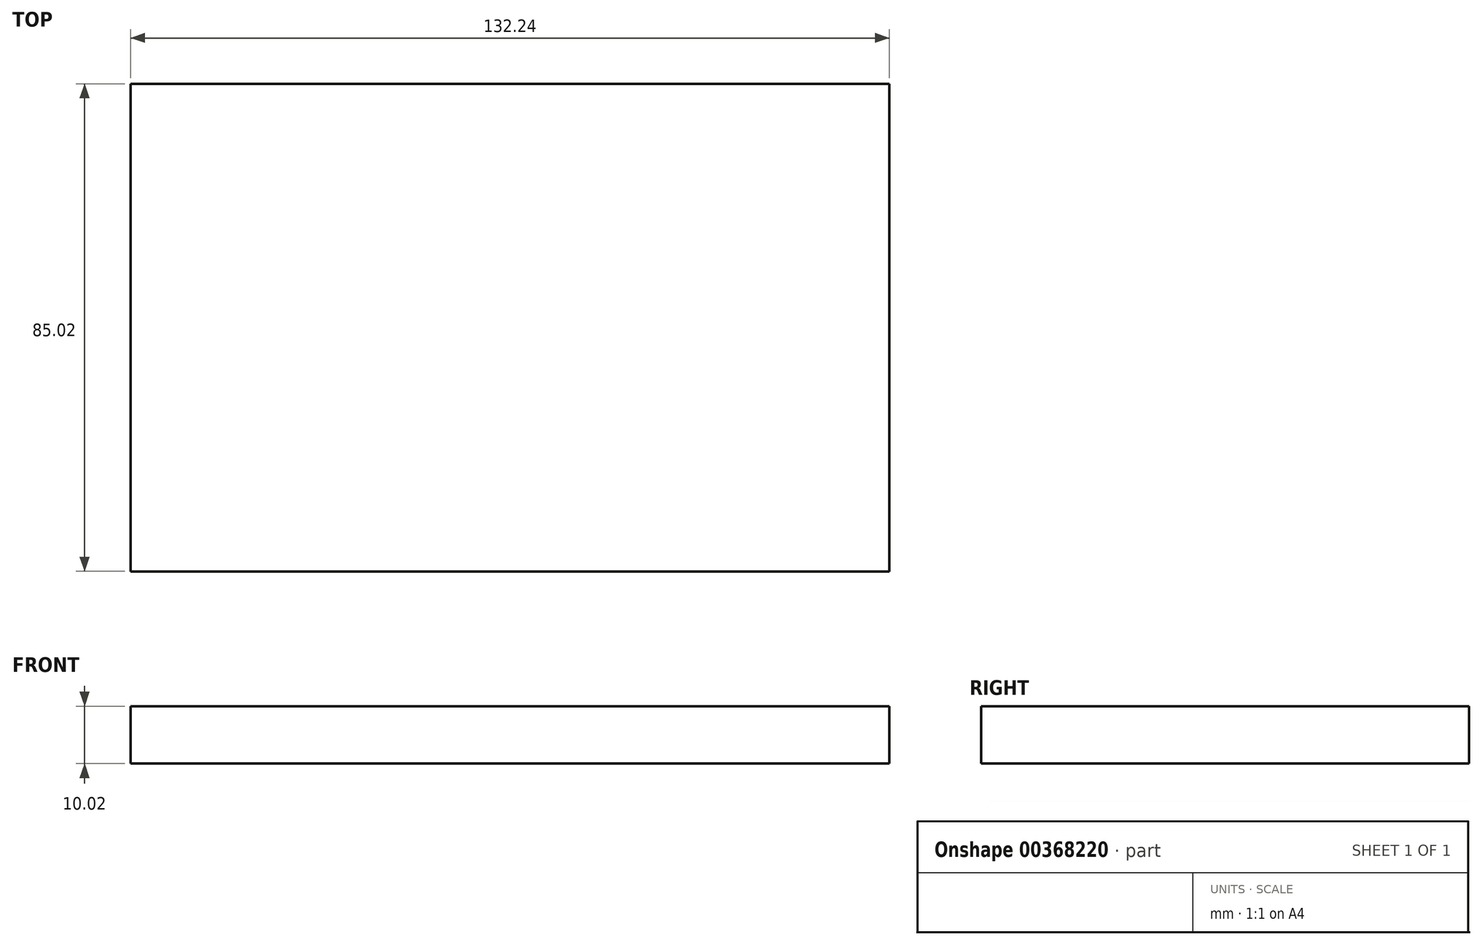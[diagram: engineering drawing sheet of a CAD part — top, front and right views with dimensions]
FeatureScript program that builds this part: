
annotation { "Feature Type Name" : "Feature", "Feature Type Description" : "" }
export const myFeature = defineFeature(function(context is Context, id is Id, definition is map)
    precondition{}
    {
        {
            var Q0;
            Q0=qCreatedBy(makeId("Top.planeOp"),FACE);
            var sketch = newSketch(context, id + "F0", { "sketchPlane" : qUnion([Q0])});
            skLineSegment(sketch, "E0.bottom", {"start": v(-66.12, 42.51) * mm, "end": v(66.12, 42.51) * mm});
            skLineSegment(sketch, "E0.top", {"start": v(-66.12, -42.51) * mm, "end": v(66.12, -42.51) * mm});
            skLineSegment(sketch, "E0.left", {"start": v(-66.12, 42.51) * mm, "end": v(-66.12, -42.51) * mm});
            skLineSegment(sketch, "E0.right", {"start": v(66.12, 42.51) * mm, "end": v(66.12, -42.51) * mm});
            skPoint(sketch, "E0.middle", {"position": v(0, 0) * mm});
            skSolve(sketch);
        }
        {
            var Q0;
            Q0 = qSketchRegion(id + "FchOqiulusQZ7VD_0", true);
            var Q1;
            Q1=makeQuery(id+"F0.imprint","IMPRINT",FACE,{"disambiguationData":[TD([[makeQuery(id+"F0.imprint","IMPRINT",EDGE,{"derivedFrom":sQuery(id+"F0.wireOp",EDGE,"E0.bottom")}),-1.0]])]});
            extrude(context, id + "F1", {"entities" : qUnion([Q0, Q1]), "depth" : 10.02 * mm});
        }
    });
